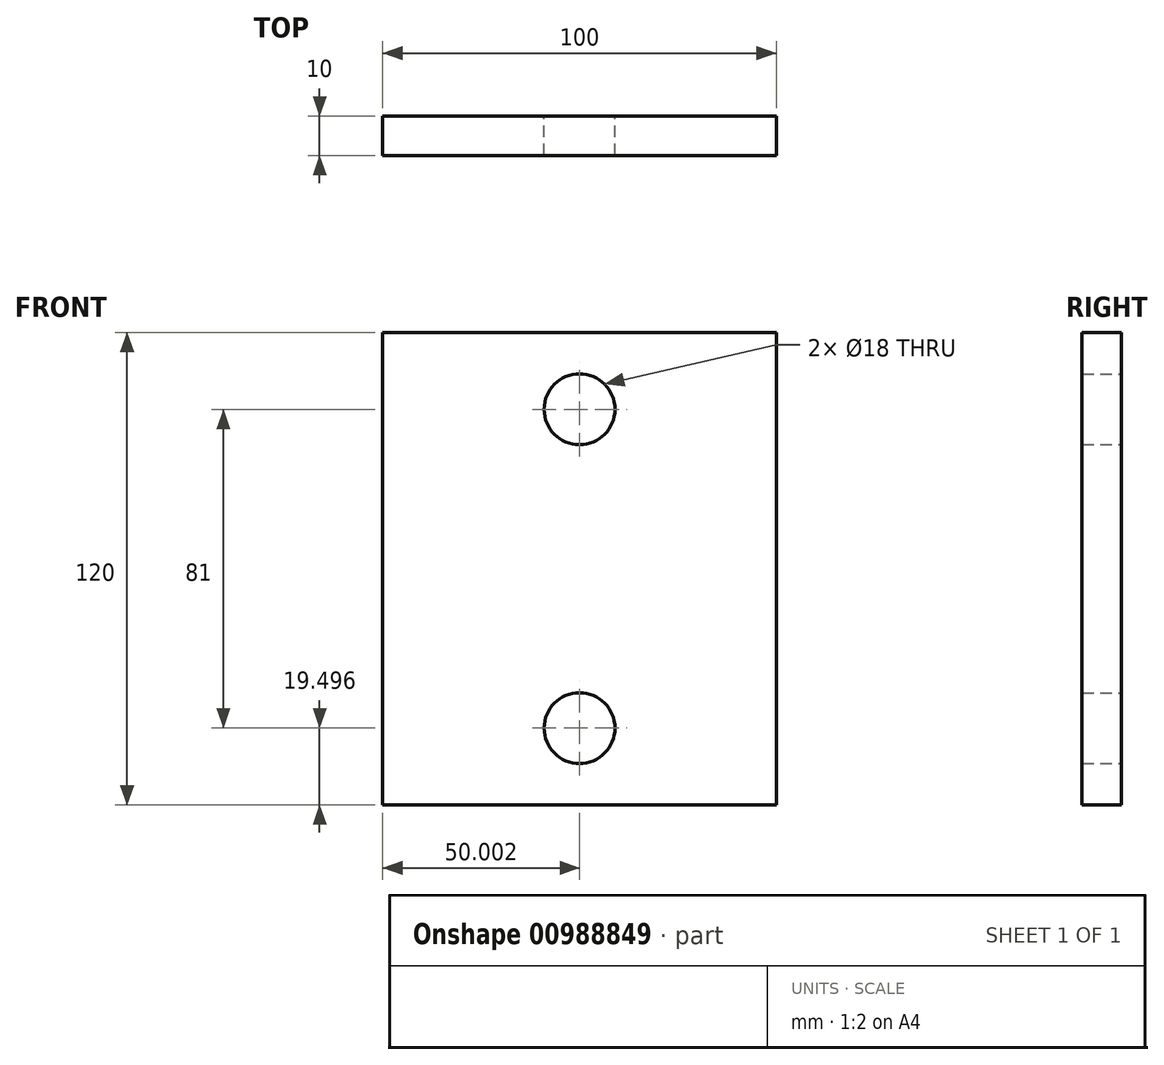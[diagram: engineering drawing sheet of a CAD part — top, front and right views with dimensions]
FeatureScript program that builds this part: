
annotation { "Feature Type Name" : "Feature", "Feature Type Description" : "" }
export const myFeature = defineFeature(function(context is Context, id is Id, definition is map)
    precondition{}
    {
        {
            var Q0;
            Q0=qCreatedBy(makeId("Front.planeOp"),FACE);
            var sketch = newSketch(context, id + "F0", { "sketchPlane" : qUnion([Q0])});
            skLineSegment(sketch, "E0.bottom", {"start": v(-92.57, 91.95) * mm, "end": v(7.43, 91.95) * mm});
            skLineSegment(sketch, "E0.top", {"start": v(-92.57, -28.05) * mm, "end": v(7.43, -28.05) * mm});
            skLineSegment(sketch, "E0.left", {"start": v(-92.57, 91.95) * mm, "end": v(-92.57, -28.05) * mm});
            skLineSegment(sketch, "E0.right", {"start": v(7.43, 91.95) * mm, "end": v(7.43, -28.05) * mm});
            skCircle(sketch, "E1", {"center": v(-42.57, 72.45) * mm, "radius": 9 * mm});
            skCircle(sketch, "E2", {"center": v(-42.57, -8.55) * mm, "radius": 9 * mm});
            skSolve(sketch);
        }
        {
            var Q0;
            Q0=makeQuery(id+"F0.imprint","IMPRINT",FACE,{"disambiguationData":[TD([[makeQuery(id+"F0.imprint","IMPRINT",EDGE,{"derivedFrom":sQuery(id+"F0.wireOp",EDGE,"E0.bottom")}),-1.0]])]});
            extrude(context, id + "F1", {"entities" : qUnion([Q0]), "depth" : 10 * mm, "offsetDistance" : 25 * mm});
        }
    });
